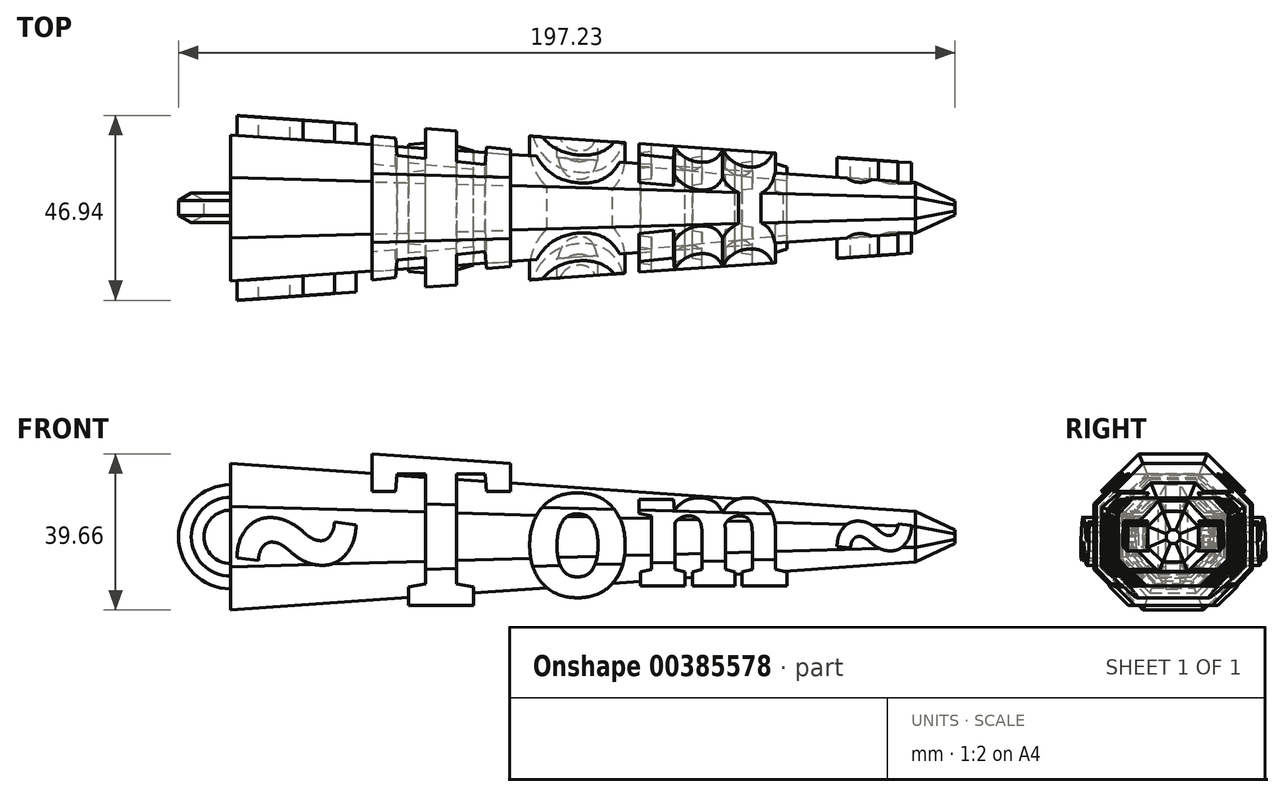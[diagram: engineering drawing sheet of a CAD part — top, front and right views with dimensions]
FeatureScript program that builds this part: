
annotation { "Feature Type Name" : "Feature", "Feature Type Description" : "" }
export const myFeature = defineFeature(function(context is Context, id is Id, definition is map)
    precondition{}
    {
        {
            assignVariable(context, id + "F0", {"name" : "hookPlane", "anyValue" : 87});
        }
        {
            assignVariable(context, id + "F1", {"name" : "halfLength", "anyValue" : 87});
        }
        {
            var Q0;
            Q0=qCreatedBy(makeId("Front.planeOp"),FACE);
            var sketch = newSketch(context, id + "F2", { "sketchPlane" : qUnion([Q0])});
            skText(sketch, "E0", { "text": "~T", "fontName": "RobotoSlab-Bold.ttf"});
            skPoint(sketch, "E1", {"position": v(-12.51, 0) * mm});
            skText(sketch, "E2", { "text": "o", "fontName": "RobotoSlab-Bold.ttf"});
            skText(sketch, "E3", { "text": "m", "fontName": "RobotoSlab-Bold.ttf"});
            skText(sketch, "E4", { "text": " ~", "fontName": "RobotoSlab-Bold.ttf"});
            skPoint(sketch, "E5", {"position": v(16.2, 0) * mm});
            skPoint(sketch, "E6", {"position": v(56.87, 0) * mm});
            skLineSegment(sketch, "E7", {"start": v(-88.1, -20) * mm, "end": v(-88.1, -51.65) * mm, "construction": true});
            skLineSegment(sketch, "E8", {"start": v(-88.1, -51.65) * mm, "end": v(88.1, -51.65) * mm, "construction": true});
            skLineSegment(sketch, "E9", {"start": v(88.1, -51.65) * mm, "end": v(88.1, -12.5) * mm, "construction": true});
            skPoint(sketch, "E10", {"position": v(0, -51.65) * mm});
            const initialGuessF2  = {"E0": [-0.0881, -0.02, 1, 0, 0.04], "E2": [-0.01251, -0.0175, 1, 0, 0.035], "E3": [0.0162, -0.015, 1, 0, 0.03], "E4": [0.05687, -0.0125, 1, 0, 0.025]};
            skSetInitialGuess(sketch, initialGuessF2);
            skSolve(sketch);
        }
        {
            var Q0;
            Q0=qSketchRegion(id+"F2",true);
            extrude(context, id + "F3", {"entities" : qUnion([Q0]), "depth" : 25 * mm, "hasSecondDirection" : true, "secondDirectionOppositeDirection" : true, "secondDirectionDepth" : 25 * mm});
        }
        {
            var Q0;
            Q0=qCreatedBy(makeId("Right.planeOp"),FACE);
            var sketch = newSketch(context, id + "F4", { "sketchPlane" : qUnion([Q0])});
            skCircle(sketch, "E11", {"center": v(0, -2.5) * mm, "radius": 12.5 * mm, "construction": true});
            skLineSegment(sketch, "E12", {"start": v(0, 19.5) * mm, "end": v(0, -8.52) * mm, "construction": true});
            skLineSegment(sketch, "E13.0", {"start": v(-5.18, 10) * mm, "end": v(5.18, 10) * mm});
            skLineSegment(sketch, "E13.1", {"start": v(5.18, 10) * mm, "end": v(12.5, 2.67) * mm});
            skLineSegment(sketch, "E13.2", {"start": v(12.5, 2.67) * mm, "end": v(12.5, -7.68) * mm});
            skLineSegment(sketch, "E13.3", {"start": v(12.5, -7.68) * mm, "end": v(5.18, -15) * mm});
            skLineSegment(sketch, "E13.4", {"start": v(5.18, -15) * mm, "end": v(-5.18, -15) * mm});
            skLineSegment(sketch, "E13.5", {"start": v(-5.18, -15) * mm, "end": v(-12.5, -7.68) * mm});
            skLineSegment(sketch, "E13.6", {"start": v(-12.5, -7.68) * mm, "end": v(-12.5, 2.67) * mm});
            skLineSegment(sketch, "E13.7", {"start": v(-12.5, 2.67) * mm, "end": v(-5.18, 10) * mm});
            skPoint(sketch, "E13.0.midPoint", {"position": v(0, 10) * mm});
            skSolve(sketch);
        }
        {
            var Q0;
            Q0=qSketchRegion(id+"F4",true);
            var Q1;
            Q1=makeQuery(id+"F3.opExtrude","SWEPT_FACE",FACE,{"disambiguationData":[OSD([sQuery(id+"F2.wireOp",EDGE,"E4.sketch_text.stroke-1")])]});
            extrude(context, id + "F5", {"entities" : qUnion([Q0]), "operationType" : NewBodyOperationType.ADD, "oppositeDirection" : true, "depth" : (getVariable(context, 'halfLength')) * mm, "hasDraft" : true, "draftAngle" : 4 * degree, "hasSecondDirection" : true, "secondDirectionOppositeDirection" : false, "secondDirectionBoundEntityFace" : qUnion([Q1]), "secondDirectionDepth" : (getVariable(context, 'halfLength')) * mm, "hasSecondDirectionDraft" : true, "secondDirectionDraftAngle" : 4 * degree, "secondDirectionDraftPullDirection" : true});
        }
        {
            var Q0;
            Q0=qCreatedBy(makeId("Right.planeOp"),FACE);
            var sketch = newSketch(context, id + "F6", { "sketchPlane" : qUnion([Q0])});
            skCircle(sketch, "E14.cCircle", {"center": v(0, -2.5) * mm, "radius": 17.5 * mm, "construction": true});
            skLineSegment(sketch, "E14.0", {"start": v(-7.25, 15) * mm, "end": v(7.25, 15) * mm});
            skLineSegment(sketch, "E14.1", {"start": v(7.25, 15) * mm, "end": v(17.5, 4.75) * mm});
            skLineSegment(sketch, "E14.2", {"start": v(17.5, 4.75) * mm, "end": v(17.5, -9.75) * mm});
            skLineSegment(sketch, "E14.3", {"start": v(17.5, -9.75) * mm, "end": v(7.25, -20) * mm});
            skLineSegment(sketch, "E14.4", {"start": v(7.25, -20) * mm, "end": v(-7.25, -20) * mm});
            skLineSegment(sketch, "E14.5", {"start": v(-7.25, -20) * mm, "end": v(-17.5, -9.75) * mm});
            skLineSegment(sketch, "E14.6", {"start": v(-17.5, -9.75) * mm, "end": v(-17.5, 4.75) * mm});
            skLineSegment(sketch, "E14.7", {"start": v(-17.5, 4.75) * mm, "end": v(-7.25, 15) * mm});
            skPoint(sketch, "E14.0.midPoint", {"position": v(0, -5.92) * mm});
            skLineSegment(sketch, "E15.bottom", {"start": v(37.5, 35) * mm, "end": v(-37.5, 35) * mm});
            skLineSegment(sketch, "E15.top", {"start": v(37.5, -40) * mm, "end": v(-37.5, -40) * mm});
            skLineSegment(sketch, "E15.left", {"start": v(37.5, 35) * mm, "end": v(37.5, -40) * mm});
            skLineSegment(sketch, "E15.right", {"start": v(-37.5, 35) * mm, "end": v(-37.5, -40) * mm});
            skLineSegment(sketch, "E16", {"start": v(0, 19.5) * mm, "end": v(0, -8.52) * mm, "construction": true});
            skSolve(sketch);
        }
        {
            var Q0;
            Q0=makeQuery(id+"F6.imprint","IMPRINT",FACE,{"disambiguationData":[TD([[makeQuery(id+"F6.imprint","IMPRINT",EDGE,{"derivedFrom":sQuery(id+"F6.wireOp",EDGE,"E14.0")}),1.0]])]});
            extrude(context, id + "F7", {"entities" : qUnion([Q0]), "operationType" : NewBodyOperationType.REMOVE, "endBound" : BoundingType.THROUGH_ALL, "depth" : 25 * mm, "hasDraft" : true, "draftAngle" : 4 * degree, "hasSecondDirection" : true, "secondDirectionBound" : SecondDirectionBoundingType.THROUGH_ALL, "secondDirectionOppositeDirection" : true, "secondDirectionDepth" : 25 * mm, "hasSecondDirectionDraft" : true, "secondDirectionDraftAngle" : 4 * degree, "secondDirectionDraftPullDirection" : true});
        }
        {
            var Q0;
            {var subQ0=sQuery(id+"F4.wireOp",EDGE,"E13.3");var subQ1=sQuery(id+"F4.wireOp",EDGE,"E13.2");var subQ2=sQuery(id+"F4.wireOp",EDGE,"E13.4");var subQ3=sQuery(id+"F4.wireOp",EDGE,"E13.5");var subQ4=sQuery(id+"F4.wireOp",EDGE,"E13.6");Q0=makeQuery(id+"F5.boolean.opBoolean","SPLIT",FACE,{"disambiguationData":[TD([makeQuery(id+"F3.opExtrude","SWEPT_FACE",FACE,{"disambiguationData":[OSD([sQuery(id+"F2.wireOp",EDGE,"E4.sketch_text.stroke-0")])]})])],"derivedFrom":makeQuery(id+"F5.opExtrude","CAP_FACE",FACE,{"disambiguationData":[OSD([sQuery(id+"F4.wireOp",EDGE,"E13.0"),sQuery(id+"F4.wireOp",EDGE,"E13.1"),subQ1,subQ0,subQ2,subQ3,subQ4,sQuery(id+"F4.wireOp",EDGE,"E13.7")])],"isStart":true})});}
            var sketch = newSketch(context, id + "F8", { "sketchPlane" : qUnion([Q0])});
            skCircle(sketch, "E17.cCircle", {"center": v(0, -2.5) * mm, "radius": 6.42 * mm, "construction": true});
            skLineSegment(sketch, "E17.0", {"start": v(-2.66, 3.91) * mm, "end": v(2.66, 3.91) * mm});
            skLineSegment(sketch, "E17.1", {"start": v(2.66, 3.91) * mm, "end": v(6.42, 0.15) * mm});
            skLineSegment(sketch, "E17.2", {"start": v(6.42, 0.15) * mm, "end": v(6.42, -5.16) * mm});
            skLineSegment(sketch, "E17.3", {"start": v(6.42, -5.16) * mm, "end": v(2.66, -8.92) * mm});
            skLineSegment(sketch, "E17.4", {"start": v(2.66, -8.92) * mm, "end": v(-2.66, -8.92) * mm});
            skLineSegment(sketch, "E17.5", {"start": v(-2.66, -8.92) * mm, "end": v(-6.42, -5.16) * mm});
            skLineSegment(sketch, "E17.6", {"start": v(-6.42, -5.16) * mm, "end": v(-6.42, 0.15) * mm});
            skLineSegment(sketch, "E17.7", {"start": v(-6.42, 0.15) * mm, "end": v(-2.66, 3.91) * mm});
            skPoint(sketch, "E17.0.midPoint", {"position": v(0, 3.91) * mm});
            skLineSegment(sketch, "E18", {"start": v(0, 19.59) * mm, "end": v(0, -20.57) * mm, "construction": true});
            skSolve(sketch);
        }
        {
            var Q0;
            Q0=qSketchRegion(id+"F8",true);
            extrude(context, id + "F9", {"entities" : qUnion([Q0]), "operationType" : NewBodyOperationType.ADD, "depth" : 10 * mm, "hasDraft" : true, "draftAngle" : 25 * degree, "draftPullDirection" : true});
        }
        {
            var Q0;
            Q0=qCreatedBy(makeId("Right.planeOp"),FACE);
            cPlane(context, id + "F10", {"entities" : qUnion([Q0]), "cplaneType" : CPlaneType.OFFSET, "offset" : (getVariable(context, 'hookPlane')) * mm, "oppositeDirection" : true, "width" : 150 * mm, "height" : 150 * mm});
        }
        {
            var Q0;
            Q0=qCreatedBy(makeId("Front.planeOp"),FACE);
            var sketch = newSketch(context, id + "F11", { "sketchPlane" : qUnion([Q0])});
            skArc(sketch, "E19", {"start": v(-80.39, 5) * mm, "mid": v(-97, -2.5) * mm, "end": v(-80.39, -10) * mm});
            skLineSegment(sketch, "E20", {"start": v(-80.39, 5) * mm, "end": v(-80.39, -10) * mm, "construction": true});
            skPoint(sketch, "E21", {"position": v(-80.39, -2.5) * mm});
            skLineSegment(sketch, "E22", {"start": v(-87, 16.08) * mm, "end": v(-87, -21.09) * mm, "construction": true});
            skLineSegment(sketch, "E23", {"start": v(-87, -2.5) * mm, "end": v(-80.39, -2.5) * mm, "construction": true});
            skSolve(sketch);
        }
        {
            var Q0;
            Q0=qCreatedBy(id+"F10.planeOp",FACE);
            var sketch = newSketch(context, id + "F12", { "sketchPlane" : qUnion([Q0])});
            skCircle(sketch, "E24.cCircle", {"center": v(0, 7.5) * mm, "radius": 3.23 * mm, "construction": true});
            skLineSegment(sketch, "E24.0", {"start": v(1.87, 4.26) * mm, "end": v(-1.87, 4.26) * mm});
            skLineSegment(sketch, "E24.1", {"start": v(-1.87, 4.26) * mm, "end": v(-3.73, 7.5) * mm});
            skLineSegment(sketch, "E24.2", {"start": v(-3.73, 7.5) * mm, "end": v(-1.87, 10.73) * mm});
            skLineSegment(sketch, "E24.3", {"start": v(-1.87, 10.73) * mm, "end": v(1.87, 10.73) * mm});
            skLineSegment(sketch, "E24.4", {"start": v(1.87, 10.73) * mm, "end": v(3.73, 7.5) * mm});
            skLineSegment(sketch, "E24.5", {"start": v(3.73, 7.5) * mm, "end": v(1.87, 4.26) * mm});
            skPoint(sketch, "E24.0.midPoint", {"position": v(0, 4.26) * mm});
            skSolve(sketch);
        }
        {
            var Q0;
            Q0=qSketchRegion(id+"F12",true);
            var Q1;
            Q1=qConstructionFilter(qBodyType(qCreatedBy(id+"F11",EDGE),BodyType.WIRE),ConstructionObject.NO);
            sweep(context, id + "F13", {"operationType" : NewBodyOperationType.ADD, "profiles" : qUnion([Q0]), "path" : qUnion([Q1])});
        }
    });
